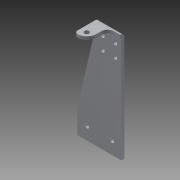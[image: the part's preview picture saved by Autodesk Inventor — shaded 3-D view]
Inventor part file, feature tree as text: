
AUTODESK INVENTOR PART (.ipt)
format: ipt  version: 2014 (Build 180170000, 170)  size: 175,104 bytes
history: native  units: in
note: dims shown in document units (in); Inventor stores cm internally (conversion verified against a paired STEP export)
features: other x3, sheet_metal_op x1, fillet x1, sketch x1
ambient origin geometry x8: Origin, YZ Plane, XZ Plane, XY Plane, X Axis, Y Axis, Z Axis, Center Point
bodies: Solid1 (feature_tree)
feature tree (6):
  sheet_metal_op  "Face1"
  fillet  "Fillet5"  Radius=4.1875in
  sketch  "Sketch1"  dims[d2=0.163in d4=0.7874in d6=1.0in d7=0.3937in d9=1.0in d11=0.0625in d22=0.5in d50=1.0in d51=1.75in d52=1.0in d53=0.375in d56=0.163in d57=0.25in d58=0.25in d59=0.7874in d61=0.5in d62=0.7874in d64=0.5in d67=0.125in d3=0.0625in]
  other  "Plate1"
  other  "Definition1"
  other  "Cut1"
